# Revit family: Bottle_Filler-Outdoor-Murdock-M-OBR4_Series
name_source: partatom
category: Plumbing Fixtures
units: mm (PartAtom-declared; Revit-internal decimal feet)

## family parameters
Cut with Voids When Loaded = No
Host = Face
OmniClass Number = 23.65.70.14.11
OmniClass Title = Drinking Fountains/Coolers
Part Type = Normal
Room Calculation Point = No
Round Connector Dimension = Use Diameter
Shared = Yes

## types (4) — shared parameters
-LOGO Customer Specified Logo / Graphics = No
A9100080-A 8 GPH remote water chiller = No
ADA Compliant = Yes
Activation = Sensor/ Push Button
Assembly Code = D2010820
BAT Battery Powered Operation = No
BCD - Bottle Counter Display = No
CW Connection = Yes
CWFU = 1.5
Compliance Certifications = Unit complies with ANSI A117.1, Public Law 111-380 (NO-LEAD), CHSC 116875 and NSF/ANSI 61, Section 9.
Default Elevation = 31 1/2"
Depth = 4"
Description = Recessed Outdoor Bottle Filler
FRA1 - Freeze resistant valve = No
Fill Rate = 1.0 GPM
HW Connection = No
Height = 26 1/4"
Inlet Diameter Connection = 1/4"
Installation Type = Recessed Wall Mounted
Length = 17 1/2"
MO Bottle filler operated by pushbutton only = No
Manufacturer = Murdock Manufacturing
Product Documentation Link = https://www.murdockmfg.com
Product Page URL = https://www.murdockmfg.com
URL = https://www.murdockmfg.com
Vent Connection = No
Voltage Nominal = 115 V
WFU = 2
Waste Connection = Yes
Waste Connection Diameter = 1 1/4"
x = 7 1/16"
zero-valued in all types: HWFU

## per-type parameters (varying)
| type | Finish | Material |
| M-OBR4 | Stainless Steel-Murdock-Brushed Satin | Stainless Steel-Murdock-Brushed Satin |
| M-OBR5 | Stainless Steel-Murdock-Powder Coated Green | Stainless Steel-Murdock-Powder Coated Green |
| M-OBR6 | Stainless Steel-Murdock-Powder Coated Red | Stainless Steel-Murdock-Powder Coated Red |
| M-OBR7 | Stainless Steel-Murdock-Powder Coated Blue | Stainless Steel-Murdock-Powder Coated Blue |

note: column(s) folded — value = type name in every type: Model

## geometry (parser evidence)
native form markers: Sweep x3
no freeform markers — native parametric forms only
